# Revit family: AD-P6T
name_source: partatom
category: Communication Devices
revit_build: Autodesk Revit 2014 (Build: 20130308_1515(x64)
units: mm (PartAtom-declared; Revit-internal decimal feet)

## types (1)
- AD-P6T
    100V Taps = 15, 30, 60
    70V Taps = 7.5, 15, 30, 60
    Coverage Horizontal = 135.00°
    Coverage Vertical = 135.00°
    Default Elevation = 0 mm
    Description = 6.5" 2-Way Pendant-Mount Loudspeaker
    Impedance = 16
    Manufacturer = QSC Audio Products, LLC
    Manufacturer URL = qsc.com
    Model = AD-P6T
    Power Handling = 60
    Product Documentation Link = http://www.qsc.com
    Product Page URL = http://www.qsc.com
    Regulatory Compliance = EN54-24: 2008, UL1480, UL2043, NFPA90, NFPA70, UL1876, RoHS, CE, UL94-V0, UL94-5VB
    SPL Max = 112
    Sensitivity = 88
    URL = http://www.qsc.com
    Weight Dimensional (kg) = 5.4
    Weight Dimensional (lb) = 11.8
    Weight Product (kg) = 4.1
    Weight Product (lb) = 9

## geometry (parser evidence)
native form markers: Blend x1, Sweep x1
no freeform markers — native parametric forms only
